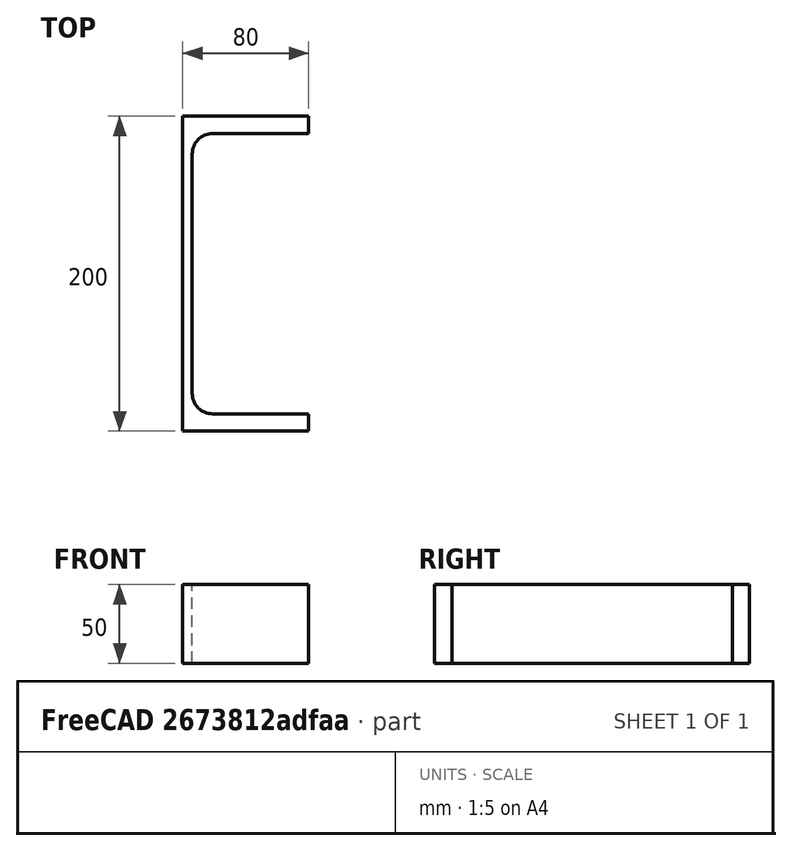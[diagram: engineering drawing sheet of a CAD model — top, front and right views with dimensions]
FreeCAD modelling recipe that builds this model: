
FCSTD DOCUMENT  (FreeCAD 0.20R29410 (Git))
Label: UPE-Profile 200 DIN1026-2 S235JR
License: All rights reserved
LicenseURL: http://en.wikipedia.org/wiki/All_rights_reserved
objects: Sketcher::SketchObject×1, Part::Extrusion×1
note: 2 computed .brp shape members not serialized (recipe doc carries the construction recipe); baked Part::Feature solids carry a one-line shape summary decoded from their .brp

FEATURE [Sketcher::SketchObject] Sketch
  FullyConstrained = true
  MapMode = 5
  sketch-geometry (10):
    g0: LineSegment StartX=6 StartY=-76 StartZ=0 EndX=6 EndY=76 EndZ=0
    g1: LineSegment StartX=19 StartY=89 StartZ=0 EndX=80 EndY=89 EndZ=0
    g2: LineSegment StartX=80 StartY=89 StartZ=0 EndX=80 EndY=100 EndZ=0
    g3: LineSegment StartX=80 StartY=-100 StartZ=0 EndX=80 EndY=-89 EndZ=0
    g4: LineSegment StartX=80 StartY=-89 StartZ=0 EndX=19 EndY=-89 EndZ=0
    g5: ArcOfCircle CenterX=19 CenterY=76 CenterZ=0 NormalX=0 NormalY=0 NormalZ=1 AngleXU=0 Radius=13 StartAngle=1.5708 EndAngle=3.14159
    g6: ArcOfCircle CenterX=19 CenterY=-76 CenterZ=0 NormalX=0 NormalY=0 NormalZ=1 AngleXU=0 Radius=13 StartAngle=3.14159 EndAngle=4.71239
    g7: LineSegment StartX=80 StartY=-100 StartZ=0 EndX=0 EndY=-100 EndZ=0
    g8: LineSegment StartX=0 StartY=-100 StartZ=0 EndX=0 EndY=100 EndZ=0
    g9: LineSegment StartX=0 StartY=100 StartZ=0 EndX=80 EndY=100 EndZ=0
  constraints (27):
    c: Vertical(g0)
    c: Coincident(g2,g1)
    c: Vertical(g2)
    c: Vertical(g3)
    c: Coincident(g4,g3)
    c: Horizontal(g4)
    c: Tangent(g1,g5) = 1.5708
    c: Tangent(g0,g5) = 1.5708
    c: Tangent(g0,g6) = 1.5708
    c: Tangent(g4,g6) = 1.5708
    c: Symmetric(g2,g3,g-1)
    c: DistanceY(g2) = 11
    c: Radius(g5) = 13
    c: Coincident(g3,g7)
    c: PointOnObject(g7,g-2)
    c: Horizontal(g7)
    c: Coincident(g7,g8)
    c: PointOnObject(g8,g-2)
    c: Coincident(g8,g9)
    c: Coincident(g9,g2)
    c: Horizontal(g9)
    c: Distance(g-1,g0) = 6
    c: DistanceX(g9,g9) = 80
    c: Horizontal(g1)
    c: Equal(g3,g2)
    c: Equal(g5,g6)
    c: DistanceY(g3,g2) = 200
FEATURE [Part::Extrusion] Extrude  label="UPE-Profile 200 DIN1026-2 S235JR"
  Base = -> Sketch
  Dir = (0,0,50)
  DirMode = 0
  FaceMakerClass = Part::FaceMakerExtrusion
  LengthFwd = 0
  LengthRev = 0
  Solid = true
  Symmetric = false
